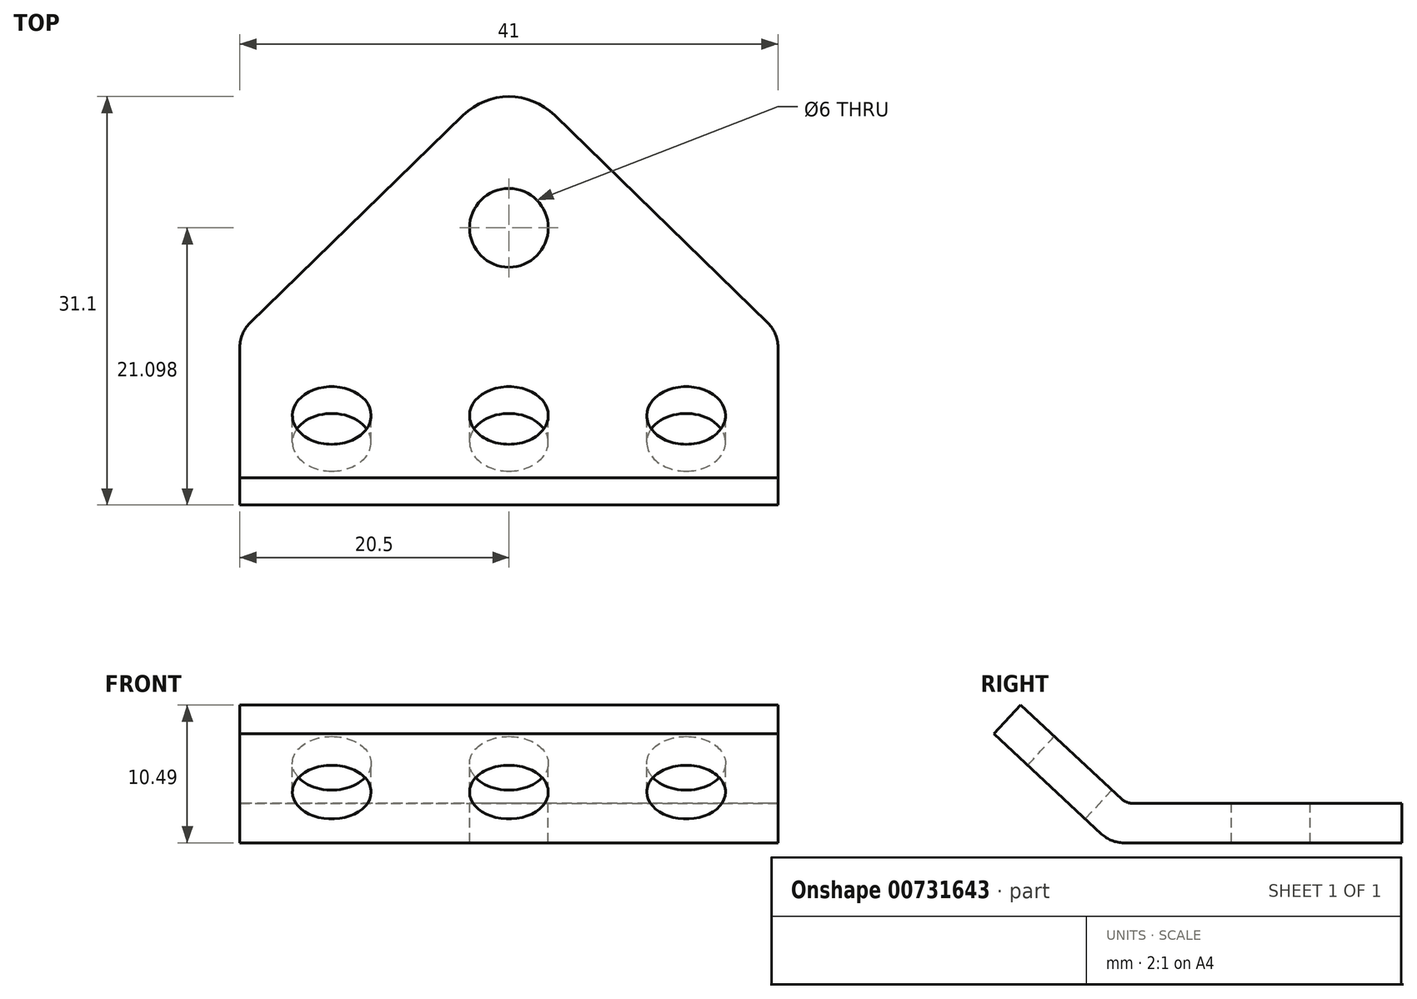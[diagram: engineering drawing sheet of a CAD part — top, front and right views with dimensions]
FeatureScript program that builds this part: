
annotation { "Feature Type Name" : "Feature", "Feature Type Description" : "" }
export const myFeature = defineFeature(function(context is Context, id is Id, definition is map)
    precondition{}
    {
        {
            var Q0;
            Q0=qCreatedBy(makeId("Top.planeOp"),FACE);
            var sketch = newSketch(context, id + "F0", { "sketchPlane" : qUnion([Q0])});
            skLineSegment(sketch, "E0", {"start": v(-3.5, -3.4) * mm, "end": v(-19.75, -19.25) * mm});
            skLineSegment(sketch, "E1", {"start": v(-20.5, -21.04) * mm, "end": v(-20.5, -22.98) * mm});
            skLineSegment(sketch, "E2", {"start": v(-20.5, -22.98) * mm, "end": v(20.5, -22.98) * mm});
            skLineSegment(sketch, "E3", {"start": v(20.5, -22.98) * mm, "end": v(20.5, -21.04) * mm});
            skLineSegment(sketch, "E4", {"start": v(19.75, -19.25) * mm, "end": v(3.5, -3.4) * mm});
            skPoint(sketch, "E5.visualSharp", {"position": v(0, 0) * mm});
            skArc(sketch, "E5.filletArc", {"start": v(3.5, -3.4) * mm, "mid": v(0, -1.98) * mm, "end": v(-3.5, -3.4) * mm});
            skPoint(sketch, "E6.visualSharp", {"position": v(-20.5, -19.98) * mm});
            skArc(sketch, "E6.filletArc", {"start": v(-19.75, -19.25) * mm, "mid": v(-20.3, -20.07) * mm, "end": v(-20.5, -21.04) * mm});
            skPoint(sketch, "E7.visualSharp", {"position": v(20.5, -19.98) * mm});
            skArc(sketch, "E7.filletArc", {"start": v(20.5, -21.04) * mm, "mid": v(20.3, -20.07) * mm, "end": v(19.75, -19.25) * mm});
            skSolve(sketch);
        }
        {
            var Q0;
            Q0 = qSketchRegion(id + "F0", true);
            extrude(context, id + "F1", {"entities" : qUnion([Q0]), "depth" : 3 * mm, "offsetDistance" : 25 * mm});
        }
        {
            var Q0;
            Q0=makeQuery(id+"F1.opExtrude","CAP_FACE",FACE,{"disambiguationData":[OSD([sQuery(id+"F0.wireOp",EDGE,"E0"),sQuery(id+"F0.wireOp",EDGE,"E1"),sQuery(id+"F0.wireOp",EDGE,"E2"),sQuery(id+"F0.wireOp",EDGE,"E3"),sQuery(id+"F0.wireOp",EDGE,"E4"),sQuery(id+"F0.wireOp",EDGE,"E5.filletArc"),sQuery(id+"F0.wireOp",EDGE,"E6.filletArc"),sQuery(id+"F0.wireOp",EDGE,"E7.filletArc")])],"isStart":false});
            var sketch = newSketch(context, id + "F2", { "sketchPlane" : qUnion([Q0])});
            skCircle(sketch, "E8", {"center": v(0, -11.98) * mm, "radius": 3 * mm});
            skSolve(sketch);
        }
        {
            var Q0;
            Q0 = qSketchRegion(id + "F2", true);
            extrude(context, id + "F3", {"entities" : qUnion([Q0]), "operationType" : NewBodyOperationType.REMOVE, "oppositeDirection" : true, "depth" : 3 * mm, "offsetDistance" : 25 * mm});
        }
        {
            var Q0;
            Q0=makeQuery(id+"F1.opExtrude","SWEPT_FACE",FACE,{"disambiguationData":[OSD([sQuery(id+"F0.wireOp",EDGE,"E1")])]});
            var sketch = newSketch(context, id + "F4", { "sketchPlane" : qUnion([Q0])});
            skLineSegment(sketch, "E9", {"start": v(22.98, 3) * mm, "end": v(31.04, 10.5) * mm});
            skLineSegment(sketch, "E10", {"start": v(31.04, 10.5) * mm, "end": v(33.08, 8.3) * mm});
            skLineSegment(sketch, "E11", {"start": v(33.08, 8.3) * mm, "end": v(24.88, 0.67) * mm});
            skLineSegment(sketch, "E12", {"start": v(23.18, 0) * mm, "end": v(22.98, 0) * mm});
            skPoint(sketch, "E13.visualSharp", {"position": v(24.16, 0) * mm});
            skArc(sketch, "E13.filletArc", {"start": v(23.18, 0) * mm, "mid": v(24.1, 0.17) * mm, "end": v(24.88, 0.67) * mm});
            skSolve(sketch);
        }
        {
            var Q0;
            Q0=makeQuery(id+"F4.imprint","IMPRINT",FACE,{"disambiguationData":[TD([[makeQuery(id+"F4.imprint","IMPRINT",EDGE,{"derivedFrom":sQuery(id+"F4.wireOp",EDGE,"E9")}),-1.0]])]});
            extrude(context, id + "F5", {"entities" : qUnion([Q0]), "operationType" : NewBodyOperationType.ADD, "depth" : -41 * mm, "offsetDistance" : 25 * mm});
        }
        {
            var Q0;
            {var subQ0=sQuery(id+"F0.wireOp",EDGE,"E2");Q0=makeQuery(id+"F5.boolean.opBoolean","MERGE",EDGE,{"derivedFrom":[makeQuery(id+"F1.opExtrude","CAP_EDGE",EDGE,{"disambiguationData":[OSD([subQ0])],"isStart":false}),makeQuery(id+"F5.opExtrude","SWEPT_EDGE",EDGE,{"disambiguationData":[OSD([sQuery(id+"F0.wireOp",EDGE,"E1"),subQ0,sQuery(id+"F4.wireOp",EDGE,"E9")])]})]});}
            fillet(context, id + "F6", {"entities" : qUnion([Q0]), "radius" : 1.25 * mm, "tangentPropagation" : true, "allowEdgeOverflow" : false});
        }
        {
            var Q0;
            Q0=makeQuery(id+"F5.opExtrude","SWEPT_FACE",FACE,{"disambiguationData":[OSD([sQuery(id+"F4.wireOp",EDGE,"E9")])]});
            var sketch = newSketch(context, id + "F7", { "sketchPlane" : qUnion([Q0])});
            skCircle(sketch, "E14", {"center": v(13.5, -23.36) * mm, "radius": 3 * mm});
            skCircle(sketch, "E15", {"center": v(0, -23.36) * mm, "radius": 3 * mm});
            skCircle(sketch, "E16", {"center": v(-13.5, -23.36) * mm, "radius": 3 * mm});
            skSolve(sketch);
        }
        {
            var Q0;
            Q0 = qSketchRegion(id + "F7", true);
            extrude(context, id + "F8", {"entities" : qUnion([Q0]), "operationType" : NewBodyOperationType.REMOVE, "oppositeDirection" : true, "depth" : 3 * mm, "offsetDistance" : 25 * mm});
        }
    });
